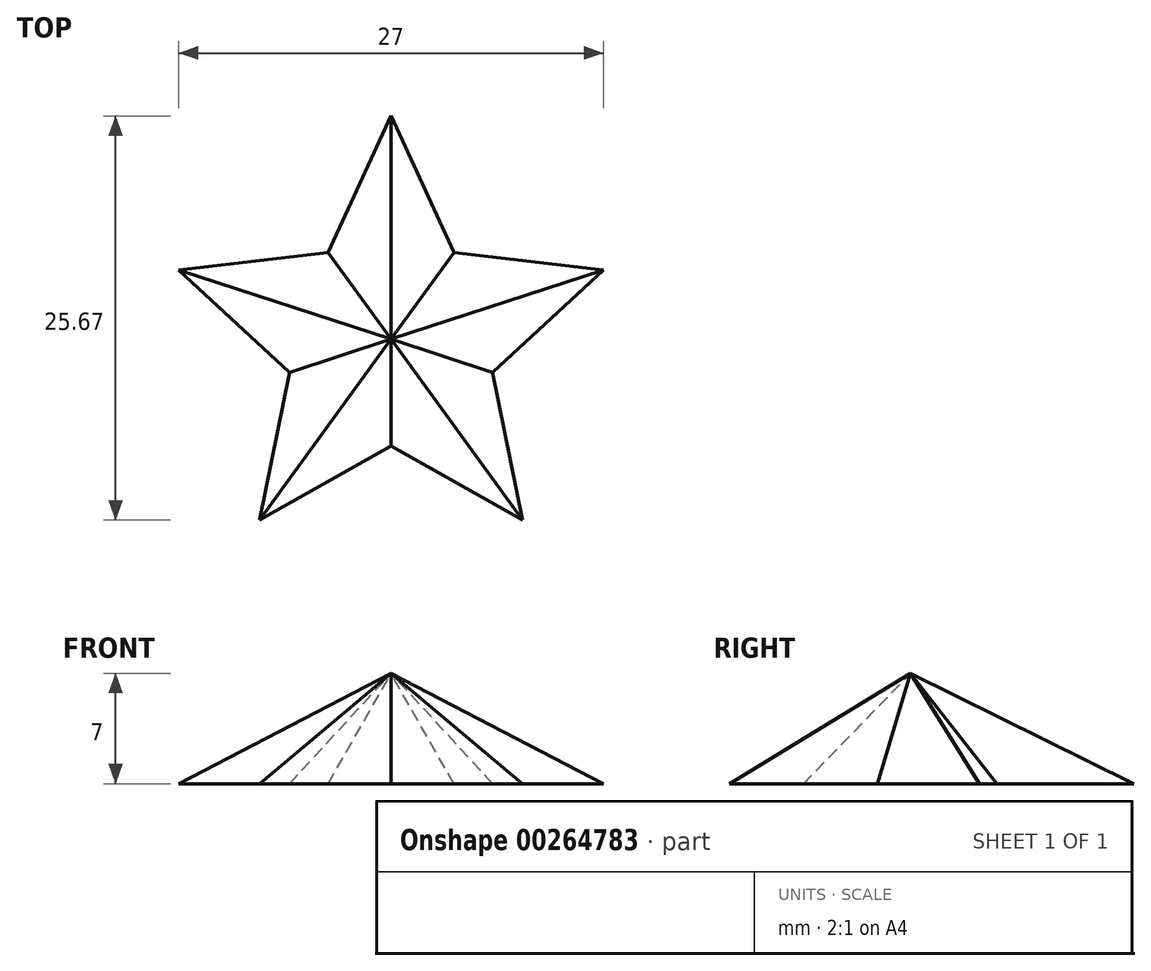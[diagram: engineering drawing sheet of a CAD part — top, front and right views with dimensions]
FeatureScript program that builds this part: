
annotation { "Feature Type Name" : "Feature", "Feature Type Description" : "" }
export const myFeature = defineFeature(function(context is Context, id is Id, definition is map)
    precondition{}
    {
        {
            var Q0;
            Q0=qCreatedBy(makeId("Top.planeOp"),FACE);
            var sketch = newSketch(context, id + "F0", { "sketchPlane" : qUnion([Q0])});
            skCircle(sketch, "E0.cCircle", {"center": v(0, 0) * mm, "radius": 11.48 * mm, "construction": true});
            skLineSegment(sketch, "E0.0", {"start": v(0, 14.2) * mm, "end": v(13.5, 4.39) * mm, "construction": true});
            skLineSegment(sketch, "E0.1", {"start": v(13.5, 4.39) * mm, "end": v(8.34, -11.48) * mm, "construction": true});
            skLineSegment(sketch, "E0.2", {"start": v(8.34, -11.48) * mm, "end": v(-8.34, -11.48) * mm, "construction": true});
            skLineSegment(sketch, "E0.3", {"start": v(-8.34, -11.48) * mm, "end": v(-13.5, 4.39) * mm, "construction": true});
            skLineSegment(sketch, "E0.4", {"start": v(-13.5, 4.39) * mm, "end": v(0, 14.2) * mm, "construction": true});
            skPoint(sketch, "E0.0.midPoint", {"position": v(6.75, 9.3) * mm});
            skLineSegment(sketch, "E1", {"start": v(-8.34, -11.48) * mm, "end": v(0, 14.2) * mm, "construction": true});
            skLineSegment(sketch, "E2", {"start": v(0, 14.2) * mm, "end": v(-8.34, -11.48) * mm, "construction": true});
            skLineSegment(sketch, "E3", {"start": v(-8.34, -11.48) * mm, "end": v(13.5, 4.39) * mm, "construction": true});
            skLineSegment(sketch, "E4", {"start": v(13.5, 4.39) * mm, "end": v(-13.5, 4.39) * mm, "construction": true});
            skLineSegment(sketch, "E5", {"start": v(-13.5, 4.39) * mm, "end": v(8.34, -11.48) * mm, "construction": true});
            skLineSegment(sketch, "E6", {"start": v(8.34, -11.48) * mm, "end": v(0, 14.2) * mm, "construction": true});
            skCircle(sketch, "E7", {"center": v(0, 0) * mm, "radius": 6.8 * mm, "construction": true});
            skLineSegment(sketch, "E8", {"start": v(-3.19, 4.39) * mm, "end": v(0, 0) * mm, "construction": true});
            skLineSegment(sketch, "E9", {"start": v(0, 0) * mm, "end": v(3.19, 4.39) * mm, "construction": true});
            skLineSegment(sketch, "E10", {"start": v(-3.19, 4.39) * mm, "end": v(-4, 5.5) * mm, "construction": true});
            skLineSegment(sketch, "E11", {"start": v(0, 14.2) * mm, "end": v(-4, 5.5) * mm});
            skLineSegment(sketch, "E12.MirrorCS", {"start": v(-13.5, 4.39) * mm, "end": v(-4, 5.5) * mm});
            skLineSegment(sketch, "E13", {"start": v(0, 0) * mm, "end": v(-5.16, -1.68) * mm, "construction": true});
            skLineSegment(sketch, "E14.MirrorCS", {"start": v(-8.34, -11.48) * mm, "end": v(0, -6.8) * mm});
            skLineSegment(sketch, "E15.MirrorCS", {"start": v(8.34, -11.48) * mm, "end": v(0, -6.8) * mm});
            skLineSegment(sketch, "E16.MirrorCS", {"start": v(13.5, 4.39) * mm, "end": v(6.46, -2.1) * mm});
            skLineSegment(sketch, "E17.MirrorCS", {"start": v(8.34, -11.48) * mm, "end": v(6.46, -2.1) * mm});
            skLineSegment(sketch, "E18", {"start": v(0, 0) * mm, "end": v(5.16, -1.68) * mm, "construction": true});
            skLineSegment(sketch, "E19.MirrorCS", {"start": v(-13.5, 4.39) * mm, "end": v(-6.46, -2.1) * mm});
            skLineSegment(sketch, "E20.MirrorCS", {"start": v(-8.34, -11.48) * mm, "end": v(-6.46, -2.1) * mm});
            skLineSegment(sketch, "E21.MirrorCS", {"start": v(13.5, 4.39) * mm, "end": v(4, 5.5) * mm});
            skLineSegment(sketch, "E22.MirrorCS", {"start": v(0, 14.2) * mm, "end": v(4, 5.5) * mm});
            skSolve(sketch);
        }
        {
            var Q0;
            Q0=qCreatedBy(makeId("Top.planeOp"),FACE);
            cPlane(context, id + "F1", {"entities" : qUnion([Q0]), "cplaneType" : CPlaneType.OFFSET, "offset" : 7 * mm, "width" : 150 * mm, "height" : 150 * mm});
        }
        {
            var Q0;
            Q0=qCreatedBy(id+"F1.planeOp",FACE);
            var sketch = newSketch(context, id + "F2", { "sketchPlane" : qUnion([Q0])});
            skPoint(sketch, "E23", {"position": v(0, 0) * mm});
            skSolve(sketch);
        }
        {
            var Q0;
            Q0=makeQuery(id+"F0.imprint","IMPRINT",FACE,{"disambiguationData":[TD([[makeQuery(id+"F0.imprint","IMPRINT",EDGE,{"derivedFrom":sQuery(id+"F0.wireOp",EDGE,"E11")}),1.0]])]});
            var Q1;
            Q1=sQuery(id+"F2.wireOp",VERTEX,"E23");
            loft(context, id + "F3", {"sheetProfilesArray" : [{ "sheetProfileEntities" : qUnion([Q0]) }, { "sheetProfileEntities" : qUnion([Q1]) }]});
        }
    });
